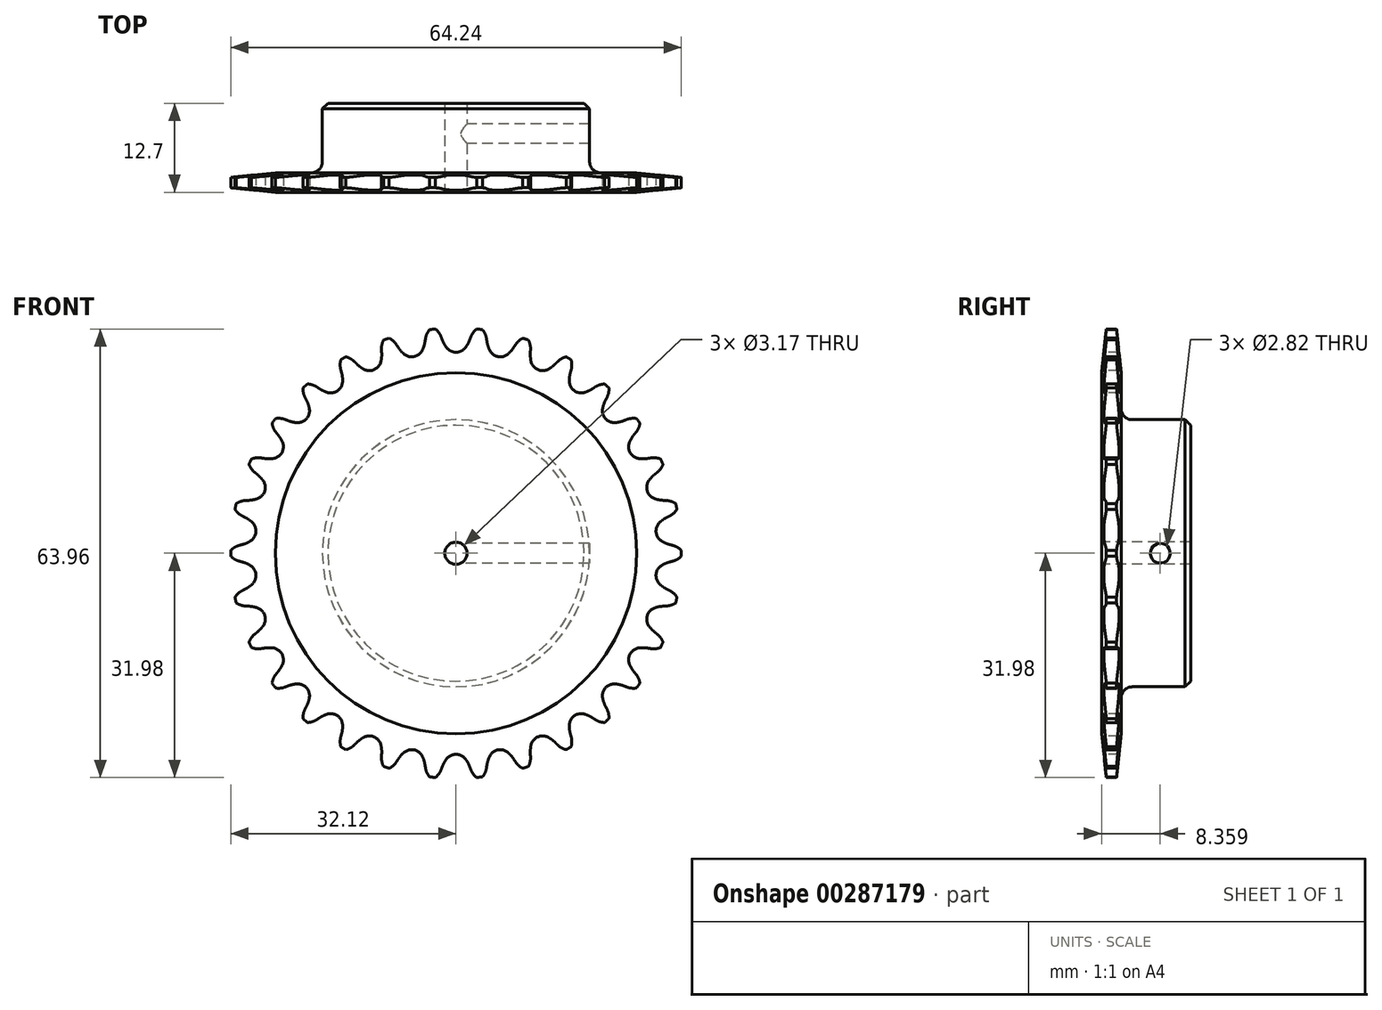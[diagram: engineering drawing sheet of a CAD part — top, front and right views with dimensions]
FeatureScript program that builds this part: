
annotation { "Feature Type Name" : "Feature", "Feature Type Description" : "" }
export const myFeature = defineFeature(function(context is Context, id is Id, definition is map)
    precondition{}
    {
        {
            var Q0;
            Q0=qCreatedBy(makeId("Right.planeOp"),FACE);
            var sketch = newSketch(context, id + "F0", { "sketchPlane" : qUnion([Q0])});
            skLineSegment(sketch, "E0", {"start": v(0, 0) * mm, "end": v(22.6, 0) * mm, "construction": true});
            skLineSegment(sketch, "E1.bottom", {"start": v(0, 19.05) * mm, "end": v(12.7, 19.05) * mm});
            skLineSegment(sketch, "E1.top", {"start": v(0, 1.59) * mm, "end": v(12.7, 1.59) * mm});
            skLineSegment(sketch, "E1.left", {"start": v(0, 19.05) * mm, "end": v(0, 1.59) * mm});
            skLineSegment(sketch, "E1.right", {"start": v(12.7, 19.05) * mm, "end": v(12.7, 1.59) * mm});
            skLineSegment(sketch, "E2.bottom", {"start": v(0, 1.59) * mm, "end": v(2.8, 1.59) * mm});
            skLineSegment(sketch, "E2.top", {"start": v(0, 32.12) * mm, "end": v(2.8, 32.12) * mm});
            skLineSegment(sketch, "E2.left", {"start": v(0, 1.59) * mm, "end": v(0, 32.12) * mm});
            skLineSegment(sketch, "E2.right", {"start": v(2.8, 1.59) * mm, "end": v(2.8, 32.12) * mm});
            skLineSegment(sketch, "E3.MirrorCS", {"start": v(0, -19.05) * mm, "end": v(0, -1.59) * mm});
            skLineSegment(sketch, "E4.MirrorCS", {"start": v(2.8, -1.59) * mm, "end": v(2.8, -32.12) * mm});
            skLineSegment(sketch, "E5.MirrorCS", {"start": v(0, -1.59) * mm, "end": v(0, -32.12) * mm});
            skLineSegment(sketch, "E6.MirrorCS", {"start": v(0, -19.05) * mm, "end": v(12.7, -19.05) * mm});
            skLineSegment(sketch, "E7.MirrorCS", {"start": v(0, -1.59) * mm, "end": v(12.7, -1.59) * mm});
            skLineSegment(sketch, "E8.MirrorCS", {"start": v(12.7, -19.05) * mm, "end": v(12.7, -1.59) * mm});
            skLineSegment(sketch, "E9.MirrorCS", {"start": v(0, -1.59) * mm, "end": v(2.8, -1.59) * mm});
            skLineSegment(sketch, "E10.MirrorCS", {"start": v(0, -32.12) * mm, "end": v(2.8, -32.12) * mm});
            skSolve(sketch);
        }
        {
            var Q0;
            {var subQ4=sQuery(id+"F0.wireOp",EDGE,"E1.top");Q0=makeQuery(id+"F0.imprint","IMPRINT",FACE,{"disambiguationData":[TD([[makeQuery(id+"F0.imprint","IMPRINT",EDGE,{"derivedFrom":subQ4}),1.0]])]});}
            var Q1;
            {var subQ5=sQuery(id+"F0.wireOp",EDGE,"E2.bottom");Q1=makeQuery(id+"F0.imprint","IMPRINT",FACE,{"disambiguationData":[TD([[makeQuery(id+"F0.imprint","IMPRINT",EDGE,{"derivedFrom":subQ5}),1.0]])]});}
            var Q2;
            {var subQ5=sQuery(id+"F0.wireOp",EDGE,"E2.top");Q2=makeQuery(id+"F0.imprint","IMPRINT",FACE,{"disambiguationData":[TD([[makeQuery(id+"F0.imprint","IMPRINT",EDGE,{"derivedFrom":subQ5}),-1.0]])]});}
            var Q3;
            Q3=sQuery(id+"F0.wireOp",EDGE,"E0");
            revolve(context, id + "F1", {"entities" : qUnion([Q0, Q1, Q2]), "axis" : qUnion([Q3]), "revolveType" : RevolveType.FULL});
        }
        {
            var Q0;
            Q0=makeQuery(id+"F1.opRevolve","SWEPT_EDGE",EDGE,{"disambiguationData":[OSD([sQuery(id+"F0.wireOp",EDGE,"E1.bottom"),sQuery(id+"F0.wireOp",EDGE,"E2.right")])]});
            fillet(context, id + "F2", {"entities" : qUnion([Q0]), "radius" : 1.59 * mm, "tangentPropagation" : true, "allowEdgeOverflow" : false});
        }
        {
            var Q0;
            Q0=makeQuery(id+"F1.opRevolve","SWEPT_EDGE",EDGE,{"disambiguationData":[OSD([sQuery(id+"F0.wireOp",EDGE,"E1.bottom"),sQuery(id+"F0.wireOp",EDGE,"E1.right")])]});
            chamfer(context, id + "F3", {"entities" : qUnion([Q0]), "width" : 0.8 * mm, "tangentPropagation" : true});
        }
        {
            var Q0;
            Q0=makeQuery(id+"F1.opRevolve","SWEPT_EDGE",EDGE,{"disambiguationData":[OSD([sQuery(id+"F0.wireOp",EDGE,"E2.top"),sQuery(id+"F0.wireOp",EDGE,"E2.left")])]});
            var Q1;
            Q1=makeQuery(id+"F1.opRevolve","SWEPT_EDGE",EDGE,{"disambiguationData":[OSD([sQuery(id+"F0.wireOp",EDGE,"E2.top"),sQuery(id+"F0.wireOp",EDGE,"E2.right")])]});
            chamfer(context, id + "F4", {"entities" : qUnion([Q0, Q1]), "chamferType" : ChamferType.TWO_OFFSETS, "width1" : 6.35 * mm, "oppositeDirection" : false, "width2" : 0.66 * mm, "tangentPropagation" : true});
        }
        {
            var Q0;
            Q0=makeQuery(id+"F1.opRevolve","SWEPT_FACE",FACE,{"disambiguationData":[OSD([sQuery(id+"F0.wireOp",EDGE,"E2.left")])]});
            var sketch = newSketch(context, id + "F5", { "sketchPlane" : qUnion([Q0])});
            skCircle(sketch, "E11", {"center": v(0, 0) * mm, "radius": 30.37 * mm, "construction": true});
            skLineSegment(sketch, "E12", {"start": v(0, 0) * mm, "end": v(0, 30.37) * mm, "construction": true});
            skLineSegment(sketch, "E13", {"start": v(0, 30.37) * mm, "end": v(73.83, 30.37) * mm, "construction": true});
            skLineSegment(sketch, "E14", {"start": v(0, 30.37) * mm, "end": v(2.1, 31.96) * mm, "construction": true});
            skLineSegment(sketch, "E15", {"start": v(2.1, 31.96) * mm, "end": v(-1.95, 30.42) * mm, "construction": true});
            skLineSegment(sketch, "E16", {"start": v(-1.95, 30.42) * mm, "end": v(-2.1, 30.84) * mm});
            skLineSegment(sketch, "E17", {"start": v(0, 0) * mm, "end": v(-3.4, 32.27) * mm, "construction": true});
            skArc(sketch, "E18", {"start": v(-3.4, 32.27) * mm, "mid": v(-6.58, 28.1) * mm, "end": v(-2.1, 30.84) * mm, "construction": true});
            skArc(sketch, "E19", {"start": v(-2.1, 30.84) * mm, "mid": v(-2.62, 31.68) * mm, "end": v(-3.4, 32.27) * mm});
            skArc(sketch, "E20", {"start": v(-1.95, 30.42) * mm, "mid": v(-1.69, 29.86) * mm, "end": v(-1.36, 29.35) * mm});
            skArc(sketch, "E21", {"start": v(-1.36, 29.35) * mm, "mid": v(5.9, 34.06) * mm, "end": v(-1.95, 30.42) * mm, "construction": true});
            skArc(sketch, "E22.0.MirrorCS", {"start": v(1.95, 30.42) * mm, "mid": v(1.69, 29.86) * mm, "end": v(1.36, 29.35) * mm});
            skLineSegment(sketch, "E23.0.MirrorCS", {"start": v(1.95, 30.42) * mm, "end": v(2.1, 30.84) * mm});
            skArc(sketch, "E24.0.MirrorCS", {"start": v(2.1, 30.84) * mm, "mid": v(2.62, 31.68) * mm, "end": v(3.4, 32.27) * mm});
            skArc(sketch, "E25", {"start": v(-1.36, 29.35) * mm, "mid": v(0, 28.68) * mm, "end": v(1.36, 29.35) * mm});
            skArc(sketch, "E26", {"start": v(1.36, 29.35) * mm, "mid": v(0, 32.07) * mm, "end": v(-1.36, 29.35) * mm, "construction": true});
            skLineSegment(sketch, "E27.trimOffspring", {"start": v(9.65, 0) * mm, "end": v(0, 25.32) * mm});
            skArc(sketch, "E28.1.0", {"start": v(-8.47, 29.73) * mm, "mid": v(-9.14, 30.44) * mm, "end": v(-10.03, 30.86) * mm});
            skLineSegment(sketch, "E28.1.1", {"start": v(-8.23, 29.35) * mm, "end": v(-8.47, 29.73) * mm});
            skArc(sketch, "E28.1.2", {"start": v(-8.23, 29.35) * mm, "mid": v(-7.86, 28.86) * mm, "end": v(-7.43, 28.43) * mm});
            skArc(sketch, "E28.1.3", {"start": v(-7.43, 28.43) * mm, "mid": v(-5.96, 28.05) * mm, "end": v(-4.78, 29) * mm});
            skArc(sketch, "E28.1.4", {"start": v(-4.42, 30.16) * mm, "mid": v(-4.56, 29.56) * mm, "end": v(-4.78, 29) * mm});
            skLineSegment(sketch, "E28.1.5", {"start": v(-4.42, 30.16) * mm, "end": v(-4.35, 30.6) * mm});
            skArc(sketch, "E28.1.6", {"start": v(-4.35, 30.6) * mm, "mid": v(-4.03, 31.53) * mm, "end": v(-3.4, 32.27) * mm});
            skArc(sketch, "E28.2.0", {"start": v(-14.47, 27.32) * mm, "mid": v(-15.27, 27.87) * mm, "end": v(-16.22, 28.1) * mm});
            skLineSegment(sketch, "E28.2.1", {"start": v(-14.15, 27) * mm, "end": v(-14.47, 27.32) * mm});
            skArc(sketch, "E28.2.2", {"start": v(-14.15, 27) * mm, "mid": v(-13.69, 26.6) * mm, "end": v(-13.18, 26.26) * mm});
            skArc(sketch, "E28.2.3", {"start": v(-13.18, 26.26) * mm, "mid": v(-11.66, 26.2) * mm, "end": v(-10.7, 27.37) * mm});
            skArc(sketch, "E28.2.4", {"start": v(-10.6, 28.58) * mm, "mid": v(-10.6, 27.97) * mm, "end": v(-10.7, 27.37) * mm});
            skLineSegment(sketch, "E28.2.5", {"start": v(-10.6, 28.58) * mm, "end": v(-10.62, 29.03) * mm});
            skArc(sketch, "E28.2.6", {"start": v(-10.62, 29.03) * mm, "mid": v(-10.5, 30) * mm, "end": v(-10.03, 30.86) * mm});
            skArc(sketch, "E28.3.0", {"start": v(-19.83, 23.71) * mm, "mid": v(-20.74, 24.09) * mm, "end": v(-21.71, 24.11) * mm});
            skLineSegment(sketch, "E28.3.1", {"start": v(-19.45, 23.47) * mm, "end": v(-19.83, 23.71) * mm});
            skArc(sketch, "E28.3.2", {"start": v(-19.45, 23.47) * mm, "mid": v(-18.92, 23.17) * mm, "end": v(-18.35, 22.95) * mm});
            skArc(sketch, "E28.3.3", {"start": v(-18.35, 22.95) * mm, "mid": v(-16.86, 23.2) * mm, "end": v(-16.16, 24.54) * mm});
            skArc(sketch, "E28.3.4", {"start": v(-16.3, 25.75) * mm, "mid": v(-16.19, 25.15) * mm, "end": v(-16.16, 24.54) * mm});
            skLineSegment(sketch, "E28.3.5", {"start": v(-16.3, 25.75) * mm, "end": v(-16.42, 26.19) * mm});
            skArc(sketch, "E28.3.6", {"start": v(-16.42, 26.19) * mm, "mid": v(-16.5, 27.16) * mm, "end": v(-16.22, 28.1) * mm});
            skArc(sketch, "E28.4.0", {"start": v(-24.33, 19.07) * mm, "mid": v(-25.3, 19.25) * mm, "end": v(-26.25, 19.07) * mm});
            skLineSegment(sketch, "E28.4.1", {"start": v(-23.9, 18.9) * mm, "end": v(-24.33, 19.07) * mm});
            skArc(sketch, "E28.4.2", {"start": v(-23.9, 18.9) * mm, "mid": v(-23.32, 18.73) * mm, "end": v(-22.72, 18.63) * mm});
            skArc(sketch, "E28.4.3", {"start": v(-22.72, 18.63) * mm, "mid": v(-21.31, 19.19) * mm, "end": v(-20.9, 20.65) * mm});
            skArc(sketch, "E28.4.4", {"start": v(-21.3, 21.8) * mm, "mid": v(-21.06, 21.24) * mm, "end": v(-20.9, 20.65) * mm});
            skLineSegment(sketch, "E28.4.5", {"start": v(-21.3, 21.8) * mm, "end": v(-21.51, 22.2) * mm});
            skArc(sketch, "E28.4.6", {"start": v(-21.51, 22.2) * mm, "mid": v(-21.79, 23.14) * mm, "end": v(-21.71, 24.11) * mm});
            skArc(sketch, "E28.5.0", {"start": v(-27.76, 13.6) * mm, "mid": v(-28.74, 13.57) * mm, "end": v(-29.64, 13.2) * mm});
            skLineSegment(sketch, "E28.5.1", {"start": v(-27.32, 13.52) * mm, "end": v(-27.76, 13.6) * mm});
            skArc(sketch, "E28.5.2", {"start": v(-27.32, 13.52) * mm, "mid": v(-26.7, 13.47) * mm, "end": v(-26.1, 13.5) * mm});
            skArc(sketch, "E28.5.3", {"start": v(-26.1, 13.5) * mm, "mid": v(-24.83, 14.34) * mm, "end": v(-24.74, 15.85) * mm});
            skArc(sketch, "E28.5.4", {"start": v(-25.37, 16.9) * mm, "mid": v(-25.02, 16.4) * mm, "end": v(-24.74, 15.85) * mm});
            skLineSegment(sketch, "E28.5.5", {"start": v(-25.37, 16.9) * mm, "end": v(-25.66, 17.25) * mm});
            skArc(sketch, "E28.5.6", {"start": v(-25.66, 17.25) * mm, "mid": v(-26.12, 18.1) * mm, "end": v(-26.25, 19.07) * mm});
            skArc(sketch, "E28.6.0", {"start": v(-29.98, 7.53) * mm, "mid": v(-30.93, 7.3) * mm, "end": v(-31.74, 6.75) * mm});
            skLineSegment(sketch, "E28.6.1", {"start": v(-29.53, 7.55) * mm, "end": v(-29.98, 7.53) * mm});
            skArc(sketch, "E28.6.2", {"start": v(-29.53, 7.55) * mm, "mid": v(-28.92, 7.62) * mm, "end": v(-28.34, 7.78) * mm});
            skArc(sketch, "E28.6.3", {"start": v(-28.34, 7.78) * mm, "mid": v(-27.27, 8.86) * mm, "end": v(-27.5, 10.36) * mm});
            skArc(sketch, "E28.6.4", {"start": v(-28.33, 11.25) * mm, "mid": v(-27.88, 10.83) * mm, "end": v(-27.5, 10.36) * mm});
            skLineSegment(sketch, "E28.6.5", {"start": v(-28.33, 11.25) * mm, "end": v(-28.68, 11.53) * mm});
            skArc(sketch, "E28.6.6", {"start": v(-28.68, 11.53) * mm, "mid": v(-29.32, 12.28) * mm, "end": v(-29.64, 13.2) * mm});
            skArc(sketch, "E28.7.0", {"start": v(-30.9, 1.13) * mm, "mid": v(-31.78, 0.7) * mm, "end": v(-32.45, 0) * mm});
            skLineSegment(sketch, "E28.7.1", {"start": v(-30.46, 1.24) * mm, "end": v(-30.9, 1.13) * mm});
            skArc(sketch, "E28.7.2", {"start": v(-30.46, 1.24) * mm, "mid": v(-29.88, 1.44) * mm, "end": v(-29.33, 1.72) * mm});
            skArc(sketch, "E28.7.3", {"start": v(-29.33, 1.72) * mm, "mid": v(-28.52, 3) * mm, "end": v(-29.05, 4.42) * mm});
            skArc(sketch, "E28.7.4", {"start": v(-30.05, 5.11) * mm, "mid": v(-29.52, 4.8) * mm, "end": v(-29.05, 4.42) * mm});
            skLineSegment(sketch, "E28.7.5", {"start": v(-30.05, 5.11) * mm, "end": v(-30.45, 5.32) * mm});
            skArc(sketch, "E28.7.6", {"start": v(-30.45, 5.32) * mm, "mid": v(-31.23, 5.91) * mm, "end": v(-31.74, 6.75) * mm});
            skArc(sketch, "E28.8.0", {"start": v(-30.45, -5.32) * mm, "mid": v(-31.23, -5.91) * mm, "end": v(-31.74, -6.75) * mm});
            skLineSegment(sketch, "E28.8.1", {"start": v(-30.05, -5.11) * mm, "end": v(-30.45, -5.32) * mm});
            skArc(sketch, "E28.8.2", {"start": v(-30.05, -5.11) * mm, "mid": v(-29.52, -4.8) * mm, "end": v(-29.05, -4.42) * mm});
            skArc(sketch, "E28.8.3", {"start": v(-29.05, -4.42) * mm, "mid": v(-28.52, -3) * mm, "end": v(-29.33, -1.72) * mm});
            skArc(sketch, "E28.8.4", {"start": v(-30.46, -1.24) * mm, "mid": v(-29.88, -1.44) * mm, "end": v(-29.33, -1.72) * mm});
            skLineSegment(sketch, "E28.8.5", {"start": v(-30.46, -1.24) * mm, "end": v(-30.9, -1.13) * mm});
            skArc(sketch, "E28.8.6", {"start": v(-30.9, -1.13) * mm, "mid": v(-31.78, -0.7) * mm, "end": v(-32.45, 0) * mm});
            skArc(sketch, "E28.9.0", {"start": v(-28.68, -11.53) * mm, "mid": v(-29.32, -12.28) * mm, "end": v(-29.64, -13.2) * mm});
            skLineSegment(sketch, "E28.9.1", {"start": v(-28.33, -11.25) * mm, "end": v(-28.68, -11.53) * mm});
            skArc(sketch, "E28.9.2", {"start": v(-28.33, -11.25) * mm, "mid": v(-27.88, -10.83) * mm, "end": v(-27.5, -10.36) * mm});
            skArc(sketch, "E28.9.3", {"start": v(-27.5, -10.36) * mm, "mid": v(-27.27, -8.86) * mm, "end": v(-28.34, -7.78) * mm});
            skArc(sketch, "E28.9.4", {"start": v(-29.53, -7.55) * mm, "mid": v(-28.92, -7.62) * mm, "end": v(-28.34, -7.78) * mm});
            skLineSegment(sketch, "E28.9.5", {"start": v(-29.53, -7.55) * mm, "end": v(-29.98, -7.53) * mm});
            skArc(sketch, "E28.9.6", {"start": v(-29.98, -7.53) * mm, "mid": v(-30.93, -7.3) * mm, "end": v(-31.74, -6.75) * mm});
            skArc(sketch, "E28.10.0", {"start": v(-25.66, -17.25) * mm, "mid": v(-26.12, -18.1) * mm, "end": v(-26.25, -19.07) * mm});
            skLineSegment(sketch, "E28.10.1", {"start": v(-25.37, -16.9) * mm, "end": v(-25.66, -17.25) * mm});
            skArc(sketch, "E28.10.2", {"start": v(-25.37, -16.9) * mm, "mid": v(-25.02, -16.4) * mm, "end": v(-24.74, -15.85) * mm});
            skArc(sketch, "E28.10.3", {"start": v(-24.74, -15.85) * mm, "mid": v(-24.83, -14.34) * mm, "end": v(-26.1, -13.5) * mm});
            skArc(sketch, "E28.10.4", {"start": v(-27.32, -13.52) * mm, "mid": v(-26.7, -13.47) * mm, "end": v(-26.1, -13.5) * mm});
            skLineSegment(sketch, "E28.10.5", {"start": v(-27.32, -13.52) * mm, "end": v(-27.76, -13.6) * mm});
            skArc(sketch, "E28.10.6", {"start": v(-27.76, -13.6) * mm, "mid": v(-28.74, -13.57) * mm, "end": v(-29.64, -13.2) * mm});
            skArc(sketch, "E28.11.0", {"start": v(-21.51, -22.2) * mm, "mid": v(-21.79, -23.14) * mm, "end": v(-21.71, -24.11) * mm});
            skLineSegment(sketch, "E28.11.1", {"start": v(-21.3, -21.8) * mm, "end": v(-21.51, -22.2) * mm});
            skArc(sketch, "E28.11.2", {"start": v(-21.3, -21.8) * mm, "mid": v(-21.06, -21.24) * mm, "end": v(-20.9, -20.65) * mm});
            skArc(sketch, "E28.11.3", {"start": v(-20.9, -20.65) * mm, "mid": v(-21.31, -19.19) * mm, "end": v(-22.72, -18.63) * mm});
            skArc(sketch, "E28.11.4", {"start": v(-23.9, -18.9) * mm, "mid": v(-23.32, -18.73) * mm, "end": v(-22.72, -18.63) * mm});
            skLineSegment(sketch, "E28.11.5", {"start": v(-23.9, -18.9) * mm, "end": v(-24.33, -19.07) * mm});
            skArc(sketch, "E28.11.6", {"start": v(-24.33, -19.07) * mm, "mid": v(-25.3, -19.25) * mm, "end": v(-26.25, -19.07) * mm});
            skArc(sketch, "E28.12.0", {"start": v(-16.42, -26.19) * mm, "mid": v(-16.5, -27.16) * mm, "end": v(-16.22, -28.1) * mm});
            skLineSegment(sketch, "E28.12.1", {"start": v(-16.3, -25.75) * mm, "end": v(-16.42, -26.19) * mm});
            skArc(sketch, "E28.12.2", {"start": v(-16.3, -25.75) * mm, "mid": v(-16.19, -25.15) * mm, "end": v(-16.16, -24.54) * mm});
            skArc(sketch, "E28.12.3", {"start": v(-16.16, -24.54) * mm, "mid": v(-16.86, -23.2) * mm, "end": v(-18.35, -22.95) * mm});
            skArc(sketch, "E28.12.4", {"start": v(-19.45, -23.47) * mm, "mid": v(-18.92, -23.17) * mm, "end": v(-18.35, -22.95) * mm});
            skLineSegment(sketch, "E28.12.5", {"start": v(-19.45, -23.47) * mm, "end": v(-19.83, -23.71) * mm});
            skArc(sketch, "E28.12.6", {"start": v(-19.83, -23.71) * mm, "mid": v(-20.74, -24.09) * mm, "end": v(-21.71, -24.11) * mm});
            skArc(sketch, "E28.13.0", {"start": v(-10.62, -29.03) * mm, "mid": v(-10.5, -30) * mm, "end": v(-10.03, -30.86) * mm});
            skLineSegment(sketch, "E28.13.1", {"start": v(-10.6, -28.58) * mm, "end": v(-10.62, -29.03) * mm});
            skArc(sketch, "E28.13.2", {"start": v(-10.6, -28.58) * mm, "mid": v(-10.6, -27.97) * mm, "end": v(-10.7, -27.37) * mm});
            skArc(sketch, "E28.13.3", {"start": v(-10.7, -27.37) * mm, "mid": v(-11.66, -26.2) * mm, "end": v(-13.18, -26.26) * mm});
            skArc(sketch, "E28.13.4", {"start": v(-14.15, -27) * mm, "mid": v(-13.69, -26.6) * mm, "end": v(-13.18, -26.26) * mm});
            skLineSegment(sketch, "E28.13.5", {"start": v(-14.15, -27) * mm, "end": v(-14.47, -27.32) * mm});
            skArc(sketch, "E28.13.6", {"start": v(-14.47, -27.32) * mm, "mid": v(-15.27, -27.87) * mm, "end": v(-16.22, -28.1) * mm});
            skArc(sketch, "E28.14.0", {"start": v(-4.35, -30.6) * mm, "mid": v(-4.03, -31.53) * mm, "end": v(-3.4, -32.27) * mm});
            skLineSegment(sketch, "E28.14.1", {"start": v(-4.42, -30.16) * mm, "end": v(-4.35, -30.6) * mm});
            skArc(sketch, "E28.14.2", {"start": v(-4.42, -30.16) * mm, "mid": v(-4.56, -29.56) * mm, "end": v(-4.78, -29) * mm});
            skArc(sketch, "E28.14.3", {"start": v(-4.78, -29) * mm, "mid": v(-5.96, -28.05) * mm, "end": v(-7.43, -28.43) * mm});
            skArc(sketch, "E28.14.4", {"start": v(-8.23, -29.35) * mm, "mid": v(-7.86, -28.86) * mm, "end": v(-7.43, -28.43) * mm});
            skLineSegment(sketch, "E28.14.5", {"start": v(-8.23, -29.35) * mm, "end": v(-8.47, -29.73) * mm});
            skArc(sketch, "E28.14.6", {"start": v(-8.47, -29.73) * mm, "mid": v(-9.14, -30.44) * mm, "end": v(-10.03, -30.86) * mm});
            skArc(sketch, "E28.15.0", {"start": v(2.1, -30.84) * mm, "mid": v(2.62, -31.68) * mm, "end": v(3.4, -32.27) * mm});
            skLineSegment(sketch, "E28.15.1", {"start": v(1.95, -30.42) * mm, "end": v(2.1, -30.84) * mm});
            skArc(sketch, "E28.15.2", {"start": v(1.95, -30.42) * mm, "mid": v(1.69, -29.86) * mm, "end": v(1.36, -29.35) * mm});
            skArc(sketch, "E28.15.3", {"start": v(1.36, -29.35) * mm, "mid": v(0, -28.68) * mm, "end": v(-1.36, -29.35) * mm});
            skArc(sketch, "E28.15.4", {"start": v(-1.95, -30.42) * mm, "mid": v(-1.69, -29.86) * mm, "end": v(-1.36, -29.35) * mm});
            skLineSegment(sketch, "E28.15.5", {"start": v(-1.95, -30.42) * mm, "end": v(-2.1, -30.84) * mm});
            skArc(sketch, "E28.15.6", {"start": v(-2.1, -30.84) * mm, "mid": v(-2.62, -31.68) * mm, "end": v(-3.4, -32.27) * mm});
            skArc(sketch, "E28.16.0", {"start": v(8.47, -29.73) * mm, "mid": v(9.14, -30.44) * mm, "end": v(10.03, -30.86) * mm});
            skLineSegment(sketch, "E28.16.1", {"start": v(8.23, -29.35) * mm, "end": v(8.47, -29.73) * mm});
            skArc(sketch, "E28.16.2", {"start": v(8.23, -29.35) * mm, "mid": v(7.86, -28.86) * mm, "end": v(7.43, -28.43) * mm});
            skArc(sketch, "E28.16.3", {"start": v(7.43, -28.43) * mm, "mid": v(5.96, -28.05) * mm, "end": v(4.78, -29) * mm});
            skArc(sketch, "E28.16.4", {"start": v(4.42, -30.16) * mm, "mid": v(4.56, -29.56) * mm, "end": v(4.78, -29) * mm});
            skLineSegment(sketch, "E28.16.5", {"start": v(4.42, -30.16) * mm, "end": v(4.35, -30.6) * mm});
            skArc(sketch, "E28.16.6", {"start": v(4.35, -30.6) * mm, "mid": v(4.03, -31.53) * mm, "end": v(3.4, -32.27) * mm});
            skArc(sketch, "E28.17.0", {"start": v(14.47, -27.32) * mm, "mid": v(15.27, -27.87) * mm, "end": v(16.22, -28.1) * mm});
            skLineSegment(sketch, "E28.17.1", {"start": v(14.15, -27) * mm, "end": v(14.47, -27.32) * mm});
            skArc(sketch, "E28.17.2", {"start": v(14.15, -27) * mm, "mid": v(13.69, -26.6) * mm, "end": v(13.18, -26.26) * mm});
            skArc(sketch, "E28.17.3", {"start": v(13.18, -26.26) * mm, "mid": v(11.66, -26.2) * mm, "end": v(10.7, -27.37) * mm});
            skArc(sketch, "E28.17.4", {"start": v(10.6, -28.58) * mm, "mid": v(10.6, -27.97) * mm, "end": v(10.7, -27.37) * mm});
            skLineSegment(sketch, "E28.17.5", {"start": v(10.6, -28.58) * mm, "end": v(10.62, -29.03) * mm});
            skArc(sketch, "E28.17.6", {"start": v(10.62, -29.03) * mm, "mid": v(10.5, -30) * mm, "end": v(10.03, -30.86) * mm});
            skArc(sketch, "E28.18.0", {"start": v(19.83, -23.71) * mm, "mid": v(20.74, -24.09) * mm, "end": v(21.71, -24.11) * mm});
            skLineSegment(sketch, "E28.18.1", {"start": v(19.45, -23.47) * mm, "end": v(19.83, -23.71) * mm});
            skArc(sketch, "E28.18.2", {"start": v(19.45, -23.47) * mm, "mid": v(18.92, -23.17) * mm, "end": v(18.35, -22.95) * mm});
            skArc(sketch, "E28.18.3", {"start": v(18.35, -22.95) * mm, "mid": v(16.86, -23.2) * mm, "end": v(16.16, -24.54) * mm});
            skArc(sketch, "E28.18.4", {"start": v(16.3, -25.75) * mm, "mid": v(16.19, -25.15) * mm, "end": v(16.16, -24.54) * mm});
            skLineSegment(sketch, "E28.18.5", {"start": v(16.3, -25.75) * mm, "end": v(16.42, -26.19) * mm});
            skArc(sketch, "E28.18.6", {"start": v(16.42, -26.19) * mm, "mid": v(16.5, -27.16) * mm, "end": v(16.22, -28.1) * mm});
            skArc(sketch, "E28.19.0", {"start": v(24.33, -19.07) * mm, "mid": v(25.3, -19.25) * mm, "end": v(26.25, -19.07) * mm});
            skLineSegment(sketch, "E28.19.1", {"start": v(23.9, -18.9) * mm, "end": v(24.33, -19.07) * mm});
            skArc(sketch, "E28.19.2", {"start": v(23.9, -18.9) * mm, "mid": v(23.32, -18.73) * mm, "end": v(22.72, -18.63) * mm});
            skArc(sketch, "E28.19.3", {"start": v(22.72, -18.63) * mm, "mid": v(21.31, -19.19) * mm, "end": v(20.9, -20.65) * mm});
            skArc(sketch, "E28.19.4", {"start": v(21.3, -21.8) * mm, "mid": v(21.06, -21.24) * mm, "end": v(20.9, -20.65) * mm});
            skLineSegment(sketch, "E28.19.5", {"start": v(21.3, -21.8) * mm, "end": v(21.51, -22.2) * mm});
            skArc(sketch, "E28.19.6", {"start": v(21.51, -22.2) * mm, "mid": v(21.79, -23.14) * mm, "end": v(21.71, -24.11) * mm});
            skArc(sketch, "E28.20.0", {"start": v(27.76, -13.6) * mm, "mid": v(28.74, -13.57) * mm, "end": v(29.64, -13.2) * mm});
            skLineSegment(sketch, "E28.20.1", {"start": v(27.32, -13.52) * mm, "end": v(27.76, -13.6) * mm});
            skArc(sketch, "E28.20.2", {"start": v(27.32, -13.52) * mm, "mid": v(26.7, -13.47) * mm, "end": v(26.1, -13.5) * mm});
            skArc(sketch, "E28.20.3", {"start": v(26.1, -13.5) * mm, "mid": v(24.83, -14.34) * mm, "end": v(24.74, -15.85) * mm});
            skArc(sketch, "E28.20.4", {"start": v(25.37, -16.9) * mm, "mid": v(25.02, -16.4) * mm, "end": v(24.74, -15.85) * mm});
            skLineSegment(sketch, "E28.20.5", {"start": v(25.37, -16.9) * mm, "end": v(25.66, -17.25) * mm});
            skArc(sketch, "E28.20.6", {"start": v(25.66, -17.25) * mm, "mid": v(26.12, -18.1) * mm, "end": v(26.25, -19.07) * mm});
            skArc(sketch, "E28.21.0", {"start": v(29.98, -7.53) * mm, "mid": v(30.93, -7.3) * mm, "end": v(31.74, -6.75) * mm});
            skLineSegment(sketch, "E28.21.1", {"start": v(29.53, -7.55) * mm, "end": v(29.98, -7.53) * mm});
            skArc(sketch, "E28.21.2", {"start": v(29.53, -7.55) * mm, "mid": v(28.92, -7.62) * mm, "end": v(28.34, -7.78) * mm});
            skArc(sketch, "E28.21.3", {"start": v(28.34, -7.78) * mm, "mid": v(27.27, -8.86) * mm, "end": v(27.5, -10.36) * mm});
            skArc(sketch, "E28.21.4", {"start": v(28.33, -11.25) * mm, "mid": v(27.88, -10.83) * mm, "end": v(27.5, -10.36) * mm});
            skLineSegment(sketch, "E28.21.5", {"start": v(28.33, -11.25) * mm, "end": v(28.68, -11.53) * mm});
            skArc(sketch, "E28.21.6", {"start": v(28.68, -11.53) * mm, "mid": v(29.32, -12.28) * mm, "end": v(29.64, -13.2) * mm});
            skArc(sketch, "E28.22.0", {"start": v(30.9, -1.13) * mm, "mid": v(31.78, -0.7) * mm, "end": v(32.45, 0) * mm});
            skLineSegment(sketch, "E28.22.1", {"start": v(30.46, -1.24) * mm, "end": v(30.9, -1.13) * mm});
            skArc(sketch, "E28.22.2", {"start": v(30.46, -1.24) * mm, "mid": v(29.88, -1.44) * mm, "end": v(29.33, -1.72) * mm});
            skArc(sketch, "E28.22.3", {"start": v(29.33, -1.72) * mm, "mid": v(28.52, -3) * mm, "end": v(29.05, -4.42) * mm});
            skArc(sketch, "E28.22.4", {"start": v(30.05, -5.11) * mm, "mid": v(29.52, -4.8) * mm, "end": v(29.05, -4.42) * mm});
            skLineSegment(sketch, "E28.22.5", {"start": v(30.05, -5.11) * mm, "end": v(30.45, -5.32) * mm});
            skArc(sketch, "E28.22.6", {"start": v(30.45, -5.32) * mm, "mid": v(31.23, -5.91) * mm, "end": v(31.74, -6.75) * mm});
            skArc(sketch, "E28.23.0", {"start": v(30.45, 5.32) * mm, "mid": v(31.23, 5.91) * mm, "end": v(31.74, 6.75) * mm});
            skLineSegment(sketch, "E28.23.1", {"start": v(30.05, 5.11) * mm, "end": v(30.45, 5.32) * mm});
            skArc(sketch, "E28.23.2", {"start": v(30.05, 5.11) * mm, "mid": v(29.52, 4.8) * mm, "end": v(29.05, 4.42) * mm});
            skArc(sketch, "E28.23.3", {"start": v(29.05, 4.42) * mm, "mid": v(28.52, 3) * mm, "end": v(29.33, 1.72) * mm});
            skArc(sketch, "E28.23.4", {"start": v(30.46, 1.24) * mm, "mid": v(29.88, 1.44) * mm, "end": v(29.33, 1.72) * mm});
            skLineSegment(sketch, "E28.23.5", {"start": v(30.46, 1.24) * mm, "end": v(30.9, 1.13) * mm});
            skArc(sketch, "E28.23.6", {"start": v(30.9, 1.13) * mm, "mid": v(31.78, 0.7) * mm, "end": v(32.45, 0) * mm});
            skArc(sketch, "E28.24.0", {"start": v(28.68, 11.53) * mm, "mid": v(29.32, 12.28) * mm, "end": v(29.64, 13.2) * mm});
            skLineSegment(sketch, "E28.24.1", {"start": v(28.33, 11.25) * mm, "end": v(28.68, 11.53) * mm});
            skArc(sketch, "E28.24.2", {"start": v(28.33, 11.25) * mm, "mid": v(27.88, 10.83) * mm, "end": v(27.5, 10.36) * mm});
            skArc(sketch, "E28.24.3", {"start": v(27.5, 10.36) * mm, "mid": v(27.27, 8.86) * mm, "end": v(28.34, 7.78) * mm});
            skArc(sketch, "E28.24.4", {"start": v(29.53, 7.55) * mm, "mid": v(28.92, 7.62) * mm, "end": v(28.34, 7.78) * mm});
            skLineSegment(sketch, "E28.24.5", {"start": v(29.53, 7.55) * mm, "end": v(29.98, 7.53) * mm});
            skArc(sketch, "E28.24.6", {"start": v(29.98, 7.53) * mm, "mid": v(30.93, 7.3) * mm, "end": v(31.74, 6.75) * mm});
            skArc(sketch, "E28.25.0", {"start": v(25.66, 17.25) * mm, "mid": v(26.12, 18.1) * mm, "end": v(26.25, 19.07) * mm});
            skLineSegment(sketch, "E28.25.1", {"start": v(25.37, 16.9) * mm, "end": v(25.66, 17.25) * mm});
            skArc(sketch, "E28.25.2", {"start": v(25.37, 16.9) * mm, "mid": v(25.02, 16.4) * mm, "end": v(24.74, 15.85) * mm});
            skArc(sketch, "E28.25.3", {"start": v(24.74, 15.85) * mm, "mid": v(24.83, 14.34) * mm, "end": v(26.1, 13.5) * mm});
            skArc(sketch, "E28.25.4", {"start": v(27.32, 13.52) * mm, "mid": v(26.7, 13.47) * mm, "end": v(26.1, 13.5) * mm});
            skLineSegment(sketch, "E28.25.5", {"start": v(27.32, 13.52) * mm, "end": v(27.76, 13.6) * mm});
            skArc(sketch, "E28.25.6", {"start": v(27.76, 13.6) * mm, "mid": v(28.74, 13.57) * mm, "end": v(29.64, 13.2) * mm});
            skArc(sketch, "E28.26.0", {"start": v(21.51, 22.2) * mm, "mid": v(21.79, 23.14) * mm, "end": v(21.71, 24.11) * mm});
            skLineSegment(sketch, "E28.26.1", {"start": v(21.3, 21.8) * mm, "end": v(21.51, 22.2) * mm});
            skArc(sketch, "E28.26.2", {"start": v(21.3, 21.8) * mm, "mid": v(21.06, 21.24) * mm, "end": v(20.9, 20.65) * mm});
            skArc(sketch, "E28.26.3", {"start": v(20.9, 20.65) * mm, "mid": v(21.31, 19.19) * mm, "end": v(22.72, 18.63) * mm});
            skArc(sketch, "E28.26.4", {"start": v(23.9, 18.9) * mm, "mid": v(23.32, 18.73) * mm, "end": v(22.72, 18.63) * mm});
            skLineSegment(sketch, "E28.26.5", {"start": v(23.9, 18.9) * mm, "end": v(24.33, 19.07) * mm});
            skArc(sketch, "E28.26.6", {"start": v(24.33, 19.07) * mm, "mid": v(25.3, 19.25) * mm, "end": v(26.25, 19.07) * mm});
            skArc(sketch, "E28.27.0", {"start": v(16.42, 26.19) * mm, "mid": v(16.5, 27.16) * mm, "end": v(16.22, 28.1) * mm});
            skLineSegment(sketch, "E28.27.1", {"start": v(16.3, 25.75) * mm, "end": v(16.42, 26.19) * mm});
            skArc(sketch, "E28.27.2", {"start": v(16.3, 25.75) * mm, "mid": v(16.19, 25.15) * mm, "end": v(16.16, 24.54) * mm});
            skArc(sketch, "E28.27.3", {"start": v(16.16, 24.54) * mm, "mid": v(16.86, 23.2) * mm, "end": v(18.35, 22.95) * mm});
            skArc(sketch, "E28.27.4", {"start": v(19.45, 23.47) * mm, "mid": v(18.92, 23.17) * mm, "end": v(18.35, 22.95) * mm});
            skLineSegment(sketch, "E28.27.5", {"start": v(19.45, 23.47) * mm, "end": v(19.83, 23.71) * mm});
            skArc(sketch, "E28.27.6", {"start": v(19.83, 23.71) * mm, "mid": v(20.74, 24.09) * mm, "end": v(21.71, 24.11) * mm});
            skArc(sketch, "E28.28.0", {"start": v(10.62, 29.03) * mm, "mid": v(10.5, 30) * mm, "end": v(10.03, 30.86) * mm});
            skLineSegment(sketch, "E28.28.1", {"start": v(10.6, 28.58) * mm, "end": v(10.62, 29.03) * mm});
            skArc(sketch, "E28.28.2", {"start": v(10.6, 28.58) * mm, "mid": v(10.6, 27.97) * mm, "end": v(10.7, 27.37) * mm});
            skArc(sketch, "E28.28.3", {"start": v(10.7, 27.37) * mm, "mid": v(11.66, 26.2) * mm, "end": v(13.18, 26.26) * mm});
            skArc(sketch, "E28.28.4", {"start": v(14.15, 27) * mm, "mid": v(13.69, 26.6) * mm, "end": v(13.18, 26.26) * mm});
            skLineSegment(sketch, "E28.28.5", {"start": v(14.15, 27) * mm, "end": v(14.47, 27.32) * mm});
            skArc(sketch, "E28.28.6", {"start": v(14.47, 27.32) * mm, "mid": v(15.27, 27.87) * mm, "end": v(16.22, 28.1) * mm});
            skArc(sketch, "E28.29.0", {"start": v(4.35, 30.6) * mm, "mid": v(4.03, 31.53) * mm, "end": v(3.4, 32.27) * mm});
            skLineSegment(sketch, "E28.29.1", {"start": v(4.42, 30.16) * mm, "end": v(4.35, 30.6) * mm});
            skArc(sketch, "E28.29.2", {"start": v(4.42, 30.16) * mm, "mid": v(4.56, 29.56) * mm, "end": v(4.78, 29) * mm});
            skArc(sketch, "E28.29.3", {"start": v(4.78, 29) * mm, "mid": v(5.96, 28.05) * mm, "end": v(7.43, 28.43) * mm});
            skArc(sketch, "E28.29.4", {"start": v(8.23, 29.35) * mm, "mid": v(7.86, 28.86) * mm, "end": v(7.43, 28.43) * mm});
            skLineSegment(sketch, "E28.29.5", {"start": v(8.23, 29.35) * mm, "end": v(8.47, 29.73) * mm});
            skArc(sketch, "E28.29.6", {"start": v(8.47, 29.73) * mm, "mid": v(9.14, 30.44) * mm, "end": v(10.03, 30.86) * mm});
            skSolve(sketch);
        }
        {
            var Q0;
            Q0 = qSketchRegion(id + "F5", true);
            extrude(context, id + "F6", {"entities" : qUnion([Q0]), "operationType" : NewBodyOperationType.INTERSECT, "oppositeDirection" : true, "depth" : 25.4 * mm});
        }
        {
            var Q0;
            Q0=qCreatedBy(makeId("Right.planeOp"),FACE);
            var sketch = newSketch(context, id + "F7", { "sketchPlane" : qUnion([Q0])});
            skCircle(sketch, "E29", {"center": v(8.36, 0) * mm, "radius": 1.41 * mm});
            skSolve(sketch);
        }
        {
            var Q0;
            Q0 = qSketchRegion(id + "F7", true);
            extrude(context, id + "F8", {"entities" : qUnion([Q0]), "operationType" : NewBodyOperationType.REMOVE, "depth" : 25.4 * mm});
        }
    });
